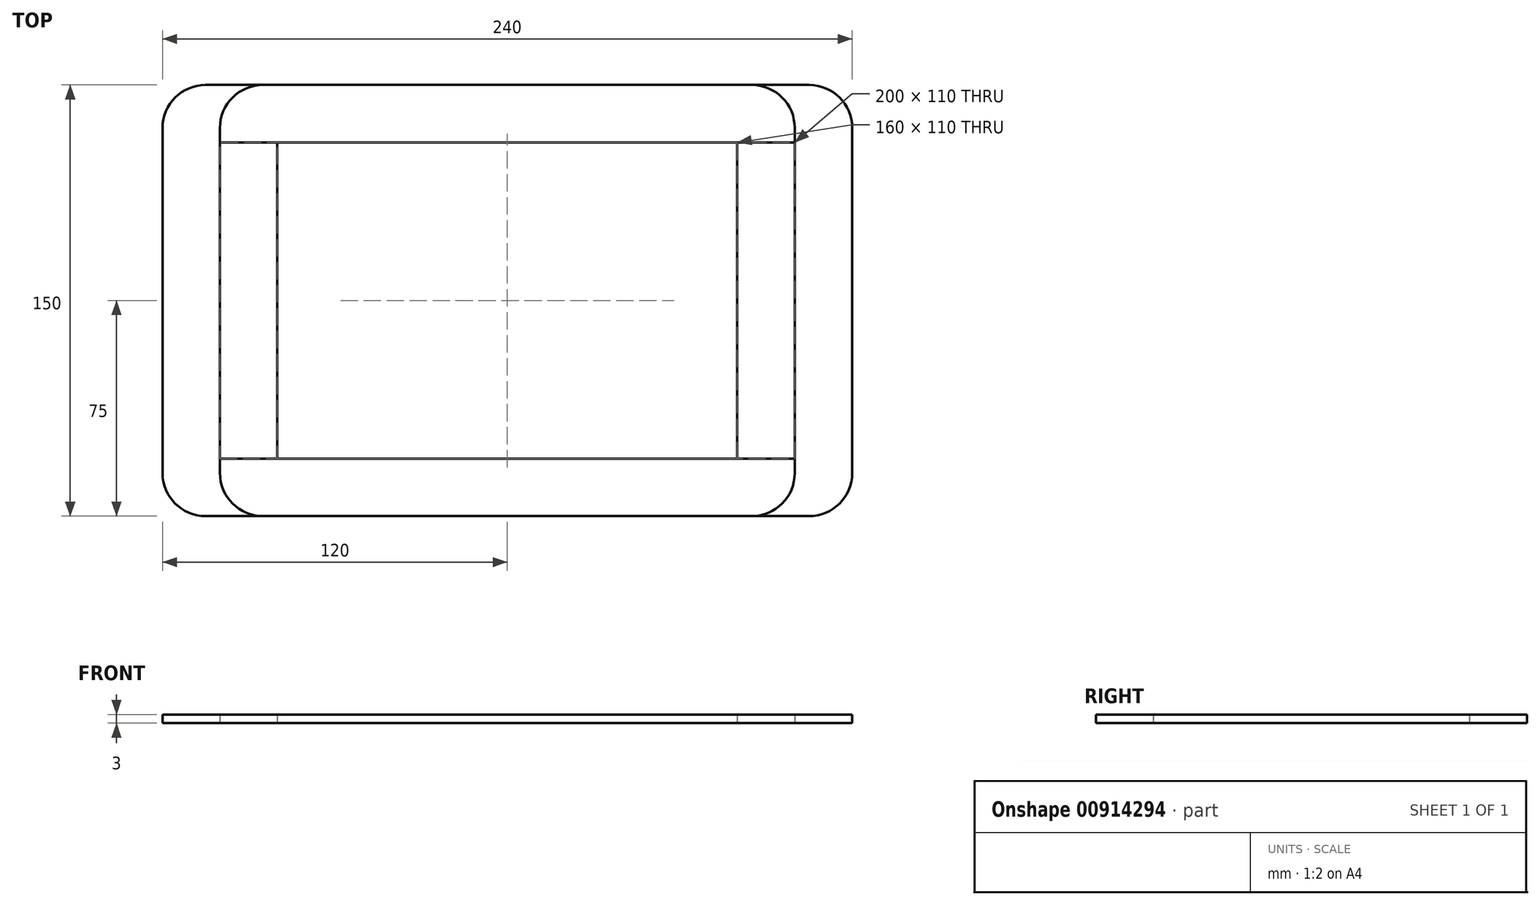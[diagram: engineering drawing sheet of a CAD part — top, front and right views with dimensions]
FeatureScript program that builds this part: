
annotation { "Feature Type Name" : "Feature", "Feature Type Description" : "" }
export const myFeature = defineFeature(function(context is Context, id is Id, definition is map)
    precondition{}
    {
        {
            var Q0;
            Q0=qCreatedBy(makeId("Top.planeOp"),FACE);
            var sketch = newSketch(context, id + "F0", { "sketchPlane" : qUnion([Q0])});
            skLineSegment(sketch, "E0.bottom", {"start": v(-80, 55) * mm, "end": v(80, 55) * mm});
            skLineSegment(sketch, "E0.top", {"start": v(-80, -55) * mm, "end": v(80, -55) * mm});
            skLineSegment(sketch, "E0.left", {"start": v(-80, 55) * mm, "end": v(-80, -55) * mm});
            skLineSegment(sketch, "E0.right", {"start": v(80, 55) * mm, "end": v(80, -55) * mm});
            skPoint(sketch, "E0.middle", {"position": v(0, 0) * mm});
            skLineSegment(sketch, "E1.bottom", {"start": v(-100, 75) * mm, "end": v(100, 75) * mm});
            skLineSegment(sketch, "E1.top", {"start": v(-100, -75) * mm, "end": v(100, -75) * mm});
            skLineSegment(sketch, "E1.left", {"start": v(-100, 75) * mm, "end": v(-100, -75) * mm});
            skLineSegment(sketch, "E1.right", {"start": v(100, 75) * mm, "end": v(100, -75) * mm});
            skSolve(sketch);
        }
        {
            var Q0;
            Q0 = qSketchRegion(id + "F0", true);
            extrude(context, id + "F1", {"entities" : qUnion([Q0]), "depth" : 3 * mm, "offsetDistance" : 25 * mm});
        }
        {
            var Q0;
            Q0=makeQuery(id+"F1.opExtrude","SWEPT_EDGE",EDGE,{"disambiguationData":[OSD([sQuery(id+"F0.wireOp",EDGE,"E1.bottom"),sQuery(id+"F0.wireOp",EDGE,"E1.left")])]});
            var Q1;
            Q1=makeQuery(id+"F1.opExtrude","SWEPT_EDGE",EDGE,{"disambiguationData":[OSD([sQuery(id+"F0.wireOp",EDGE,"E1.bottom"),sQuery(id+"F0.wireOp",EDGE,"E1.right")])]});
            var Q2;
            Q2=makeQuery(id+"F1.opExtrude","SWEPT_EDGE",EDGE,{"disambiguationData":[OSD([sQuery(id+"F0.wireOp",EDGE,"E1.top"),sQuery(id+"F0.wireOp",EDGE,"E1.right")])]});
            var Q3;
            Q3=makeQuery(id+"F1.opExtrude","SWEPT_EDGE",EDGE,{"disambiguationData":[OSD([sQuery(id+"F0.wireOp",EDGE,"E1.top"),sQuery(id+"F0.wireOp",EDGE,"E1.left")])]});
            fillet(context, id + "F2", {"entities" : qUnion([Q0, Q1, Q2, Q3]), "tangentPropagation" : true, "radius" : 15 * mm, "defaultsChanged" : true, "vertexSettings" : [], "allowEdgeOverflow" : false});
        }
        {
            var Q0;
            Q0=qCreatedBy(makeId("Top.planeOp"),FACE);
            var sketch = newSketch(context, id + "F3", { "sketchPlane" : qUnion([Q0])});
            skLineSegment(sketch, "E2.bottom", {"start": v(-100, 55) * mm, "end": v(100, 55) * mm});
            skLineSegment(sketch, "E2.top", {"start": v(-100, -55) * mm, "end": v(100, -55) * mm});
            skLineSegment(sketch, "E2.left", {"start": v(-100, 55) * mm, "end": v(-100, -55) * mm});
            skLineSegment(sketch, "E2.right", {"start": v(100, 55) * mm, "end": v(100, -55) * mm});
            skPoint(sketch, "E2.middle", {"position": v(0, 0) * mm});
            skLineSegment(sketch, "E3.bottom", {"start": v(120, -75) * mm, "end": v(-120, -75) * mm});
            skLineSegment(sketch, "E3.top", {"start": v(120, 75) * mm, "end": v(-120, 75) * mm});
            skLineSegment(sketch, "E3.left", {"start": v(120, -75) * mm, "end": v(120, 75) * mm});
            skLineSegment(sketch, "E3.right", {"start": v(-120, -75) * mm, "end": v(-120, 75) * mm});
            skSolve(sketch);
        }
        {
            var Q0;
            Q0 = qSketchRegion(id + "F3", true);
            extrude(context, id + "F4", {"entities" : qUnion([Q0]), "depth" : 3 * mm, "offsetDistance" : 25 * mm});
        }
        {
            var Q0;
            Q0=makeQuery(id+"F4.opExtrude","SWEPT_EDGE",EDGE,{"disambiguationData":[OSD([sQuery(id+"F3.wireOp",EDGE,"E3.top"),sQuery(id+"F3.wireOp",EDGE,"E3.right")])]});
            var Q1;
            Q1=makeQuery(id+"F4.opExtrude","SWEPT_EDGE",EDGE,{"disambiguationData":[OSD([sQuery(id+"F3.wireOp",EDGE,"E3.bottom"),sQuery(id+"F3.wireOp",EDGE,"E3.right")])]});
            var Q2;
            Q2=makeQuery(id+"F4.opExtrude","SWEPT_EDGE",EDGE,{"disambiguationData":[OSD([sQuery(id+"F3.wireOp",EDGE,"E3.bottom"),sQuery(id+"F3.wireOp",EDGE,"E3.left")])]});
            var Q3;
            Q3=makeQuery(id+"F4.opExtrude","SWEPT_EDGE",EDGE,{"disambiguationData":[OSD([sQuery(id+"F3.wireOp",EDGE,"E3.top"),sQuery(id+"F3.wireOp",EDGE,"E3.left")])]});
            fillet(context, id + "F5", {"entities" : qUnion([Q0, Q1, Q2, Q3]), "tangentPropagation" : true, "radius" : 15 * mm, "defaultsChanged" : true, "vertexSettings" : [], "allowEdgeOverflow" : false});
        }
    });
